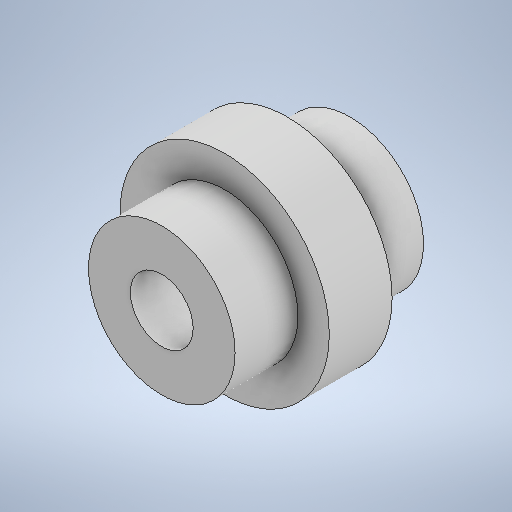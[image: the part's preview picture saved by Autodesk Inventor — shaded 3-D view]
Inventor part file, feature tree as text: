
AUTODESK INVENTOR PART (.ipt)
format: ipt  version: 2025.1 (Build 291241000, 241)  size: 281,600 bytes
history: native  units: mm
features: sketch x2, revolve x1, hole x1
ambient origin geometry x8: Origin, YZ Plane, XZ Plane, XY Plane, X Axis, Y Axis, Z Axis, Center Point
bodies: Solid1 (feature_tree)
feature tree (4):
  revolve  "Revolution1"  [1 undecoded]
  hole  "Hole1"  [1 undecoded]
  sketch  "Sketch1"  dims[d0=3.0mm d1=3.0mm]
  sketch  "Sketch2"  dims[d2=3.0mm d3=7.0mm d4=10.0mm d5=90.0deg d6=3.0mm d7=6.0mm d8=6.0mm d9=2.0mm d10=90.0deg d11=8.0mm d12=0.0mm]
note: 2 required parameter values undecoded (feature->parameter linkage not recoverable at this tier; creation-order binding heuristic only, values carry confidence <= 0.55)